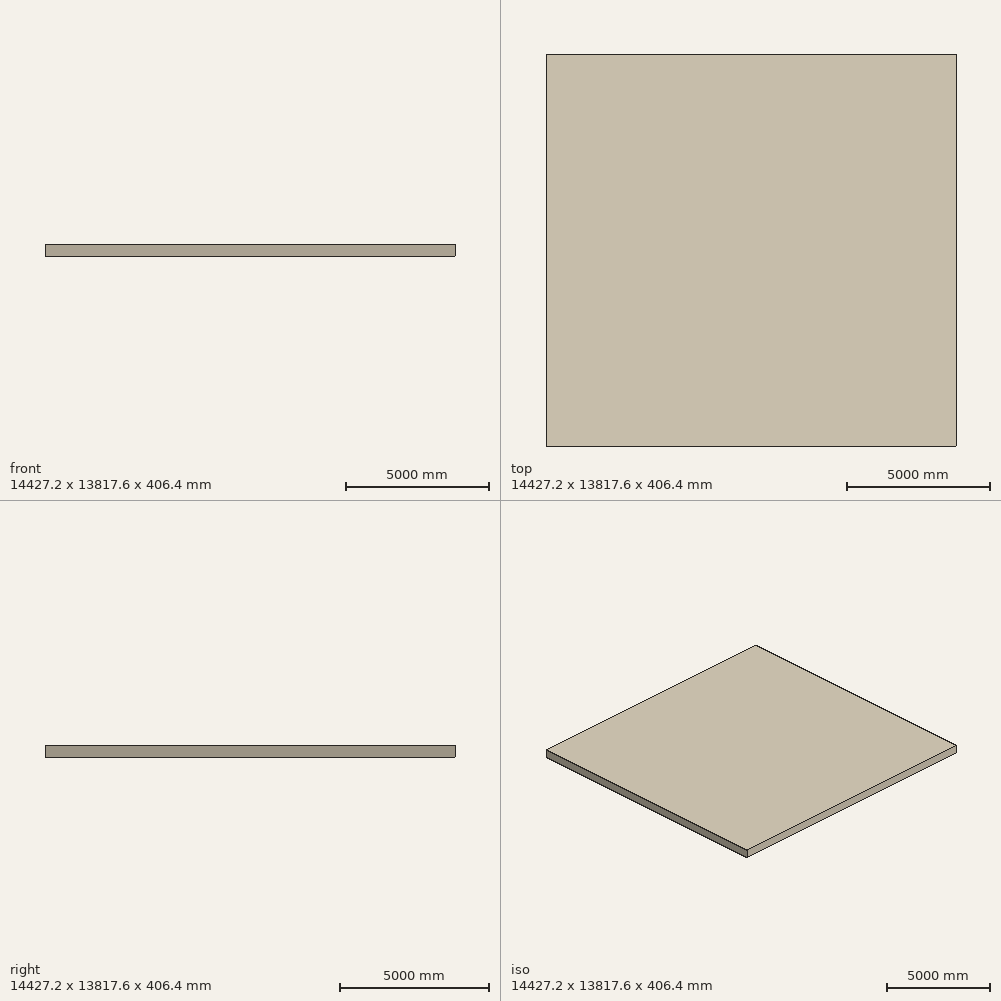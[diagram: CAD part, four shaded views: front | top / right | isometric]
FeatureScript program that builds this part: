
annotation { "Feature Type Name" : "Feature", "Feature Type Description" : "" }
export const myFeature = defineFeature(function(context is Context, id is Id, definition is map)
    precondition{}
    {
        {
            var Q0;
            Q0=qCreatedBy(makeId("Top.planeOp"),FACE);
            var sketch = newSketch(context, id + "F0", { "sketchPlane" : qUnion([Q0])});
            skLineSegment(sketch, "E0.bottom", {"start": v(-13514.16, 6918.56) * mm, "end": v(913.04, 6918.56) * mm});
            skLineSegment(sketch, "E0.top", {"start": v(-13514.16, -6899.04) * mm, "end": v(913.04, -6899.04) * mm});
            skLineSegment(sketch, "E0.left", {"start": v(-13514.16, 6918.56) * mm, "end": v(-13514.16, -6899.04) * mm});
            skLineSegment(sketch, "E0.right", {"start": v(913.04, 6918.56) * mm, "end": v(913.04, -6899.04) * mm});
            skSolve(sketch);
        }
        {
            var Q0;
            Q0 = qSketchRegion(id + "F0", true);
            extrude(context, id + "F1", {"entities" : qUnion([Q0]), "depth" : 406.4 * mm, "offsetDistance" : 25.4 * mm});
        }
    });
